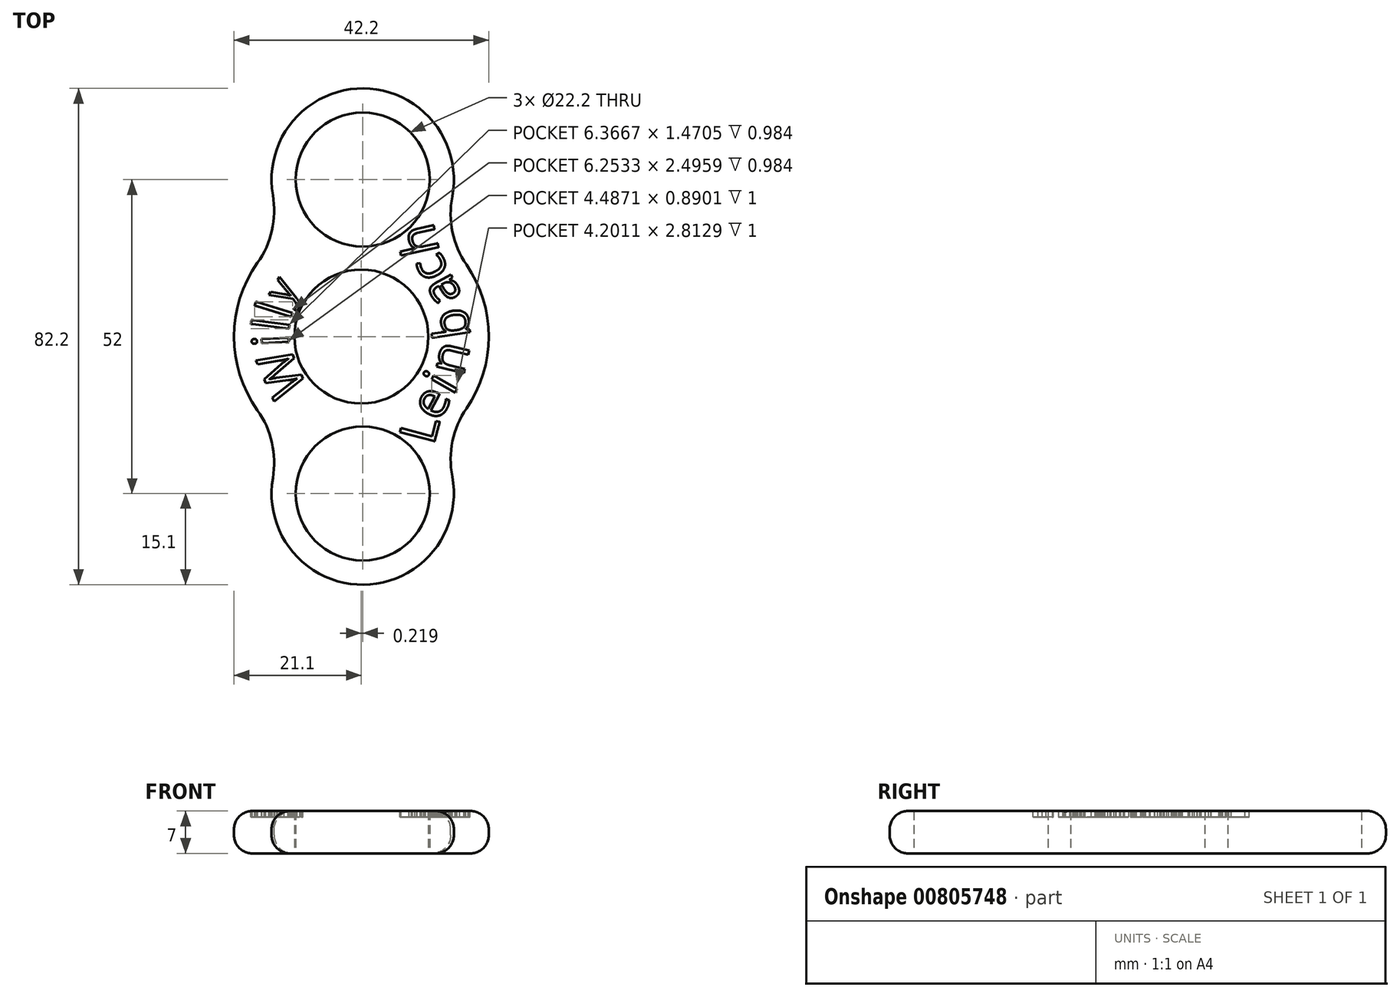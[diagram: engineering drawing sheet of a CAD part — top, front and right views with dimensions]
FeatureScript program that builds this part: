
annotation { "Feature Type Name" : "Feature", "Feature Type Description" : "" }
export const myFeature = defineFeature(function(context is Context, id is Id, definition is map)
    precondition{}
    {
        {
            var Q0;
            Q0=qCreatedBy(makeId("Top.planeOp"),FACE);
            var sketch = newSketch(context, id + "F0", { "sketchPlane" : qUnion([Q0])});
            skCircle(sketch, "E0", {"center": v(0, 0) * mm, "radius": 11.1 * mm});
            skCircle(sketch, "E1", {"center": v(0.22, 26) * mm, "radius": 11.1 * mm});
            skCircle(sketch, "E2", {"center": v(0.22, -26) * mm, "radius": 11.1 * mm});
            skCircle(sketch, "E3.0", {"center": v(0.22, 26) * mm, "radius": 15.1 * mm, "construction": true});
            skCircle(sketch, "E4.0", {"center": v(0.22, -26) * mm, "radius": 15.1 * mm, "construction": true});
            skCircle(sketch, "E5.0", {"center": v(0, 0) * mm, "radius": 21.1 * mm, "construction": true});
            skArc(sketch, "E6", {"start": v(-12.1, 17.28) * mm, "mid": v(0.35, 41.1) * mm, "end": v(12.4, 17.07) * mm});
            skArc(sketch, "E7", {"start": v(12.4, 17.07) * mm, "mid": v(21.1, 0) * mm, "end": v(12.4, -17.07) * mm});
            skArc(sketch, "E8", {"start": v(12.4, -17.07) * mm, "mid": v(0.35, -41.1) * mm, "end": v(-12.1, -17.28) * mm});
            skArc(sketch, "E9", {"start": v(-12.1, -17.28) * mm, "mid": v(-21.1, 0) * mm, "end": v(-12.1, 17.28) * mm});
            skSolve(sketch);
        }
        {
            var Q0;
            Q0=makeQuery(id+"F0.imprint","IMPRINT",FACE,{"disambiguationData":[TD([[makeQuery(id+"F0.imprint","IMPRINT",EDGE,{"derivedFrom":sQuery(id+"F0.wireOp",EDGE,"E0")}),-1.0]])]});
            extrude(context, id + "F1", {"entities" : qUnion([Q0]), "depth" : 7 * mm, "offsetDistance" : 25 * mm});
        }
        {
            var Q0;
            Q0=makeQuery(id+"F1.opExtrude","SWEPT_EDGE",EDGE,{"disambiguationData":[OSD([sQuery(id+"F0.wireOp",EDGE,"E6"),sQuery(id+"F0.wireOp",EDGE,"E9")])]});
            var Q1;
            Q1=makeQuery(id+"F1.opExtrude","SWEPT_EDGE",EDGE,{"disambiguationData":[OSD([sQuery(id+"F0.wireOp",EDGE,"E8"),sQuery(id+"F0.wireOp",EDGE,"E9")])]});
            var Q2;
            Q2=makeQuery(id+"F1.opExtrude","SWEPT_EDGE",EDGE,{"disambiguationData":[OSD([sQuery(id+"F0.wireOp",EDGE,"E7"),sQuery(id+"F0.wireOp",EDGE,"E8")])]});
            var Q3;
            Q3=makeQuery(id+"F1.opExtrude","SWEPT_EDGE",EDGE,{"disambiguationData":[OSD([sQuery(id+"F0.wireOp",EDGE,"E6"),sQuery(id+"F0.wireOp",EDGE,"E7")])]});
            fillet(context, id + "F2", {"entities" : qUnion([Q0, Q1, Q2, Q3]), "radius" : 15 * mm, "tangentPropagation" : true, "allowEdgeOverflow" : false});
        }
        {
            var Q0;
            Q0=makeQuery(id+"F1.opExtrude","CAP_EDGE",EDGE,{"disambiguationData":[OSD([sQuery(id+"F0.wireOp",EDGE,"E9")])],"isStart":false});
            var Q1;
            Q1=makeQuery(id+"F1.opExtrude","CAP_EDGE",EDGE,{"disambiguationData":[OSD([sQuery(id+"F0.wireOp",EDGE,"E7")])],"isStart":true});
            fillet(context, id + "F3", {"entities" : qUnion([Q0, Q1]), "radius" : 3 * mm, "tangentPropagation" : true, "allowEdgeOverflow" : false});
        }
        {
            var Q0;
            Q0=makeQuery(id+"F1.opExtrude","CAP_FACE",FACE,{"disambiguationData":[OSD([sQuery(id+"F0.wireOp",EDGE,"E0"),sQuery(id+"F0.wireOp",EDGE,"E1"),sQuery(id+"F0.wireOp",EDGE,"E2"),sQuery(id+"F0.wireOp",EDGE,"E6"),sQuery(id+"F0.wireOp",EDGE,"E7"),sQuery(id+"F0.wireOp",EDGE,"E8"),sQuery(id+"F0.wireOp",EDGE,"E9")])],"isStart":false});
            var sketch = newSketch(context, id + "F4", { "sketchPlane" : qUnion([Q0])});
            skText(sketch, "E10", { "text": "W", "fontName": "OpenSans-Regular.ttf"});
            skText(sketch, "E11", { "text": "i", "fontName": "OpenSans-Regular.ttf"});
            skText(sketch, "E12", { "text": "l", "fontName": "OpenSans-Regular.ttf"});
            skText(sketch, "E13", { "text": "l", "fontName": "OpenSans-Regular.ttf"});
            skText(sketch, "E14", { "text": "y", "fontName": "OpenSans-Regular.ttf"});
            const initialGuessF4  = {"E10": [-0.00898, -0.00847, -0.40537, 0.91415, 0.006], "E11": [-0.01201, -0.00158, -0.04824, 0.99884, 0.006], "E12": [-0.0121, 0.00057, 0.12637, 0.99198, 0.006], "E13": [-0.01183, 0.0026, 0.2921, 0.9564, 0.006], "E14": [-0.01215, 0.005, 0.50986, 0.86026, 0.005]};
            skSetInitialGuess(sketch, initialGuessF4);
            skSolve(sketch);
        }
        {
            var Q0;
            Q0=makeQuery(id+"F4.imprint","IMPRINT",FACE,{"disambiguationData":[TD([[makeQuery(id+"F4.imprint","IMPRINT",EDGE,{"derivedFrom":sQuery(id+"F4.wireOp",EDGE,"E10.sketch_text.stroke-0")}),-1.0]])]});
            var Q1;
            Q1=makeQuery(id+"F4.imprint","IMPRINT",FACE,{"disambiguationData":[TD([[makeQuery(id+"F4.imprint","IMPRINT",EDGE,{"derivedFrom":sQuery(id+"F4.wireOp",EDGE,"E11.sketch_text.stroke-0")}),-1.0]])]});
            var Q2;
            {var subQ0=sQuery(id+"F4.wireOp",EDGE,"E12.sketch_text.stroke-0");Q2=makeQuery(id+"F4.imprint","IMPRINT",FACE,{"disambiguationData":[TD([[makeQuery(id+"F4.imprint","IMPRINT",EDGE,{"derivedFrom":subQ0}),-1.0]])]});}
            var Q3;
            {var subQ0=sQuery(id+"F4.wireOp",EDGE,"E12.sketch_text.stroke-2");Q3=makeQuery(id+"F4.imprint","IMPRINT",FACE,{"disambiguationData":[TD([[makeQuery(id+"F4.imprint","IMPRINT",EDGE,{"derivedFrom":subQ0}),-1.0]])]});}
            var Q4;
            {var subQ0=sQuery(id+"F4.wireOp",EDGE,"E13.sketch_text.stroke-2");Q4=makeQuery(id+"F4.imprint","IMPRINT",FACE,{"disambiguationData":[TD([[makeQuery(id+"F4.imprint","IMPRINT",EDGE,{"derivedFrom":subQ0}),-1.0]])]});}
            var Q5;
            {var subQ0=sQuery(id+"F4.wireOp",EDGE,"E13.sketch_text.stroke-0");Q5=makeQuery(id+"F4.imprint","IMPRINT",FACE,{"disambiguationData":[TD([[makeQuery(id+"F4.imprint","IMPRINT",EDGE,{"derivedFrom":subQ0}),-1.0]])]});}
            var Q6;
            Q6=makeQuery(id+"F4.imprint","IMPRINT",FACE,{"disambiguationData":[TD([[makeQuery(id+"F4.imprint","IMPRINT",EDGE,{"derivedFrom":sQuery(id+"F4.wireOp",EDGE,"E14.sketch_text.stroke-0")}),-1.0]])]});
            var Q7;
            {var subQ6=sQuery(id+"F4.wireOp",EDGE,"E11.sketch_text.stroke-4");Q7=makeQuery(id+"F4.imprint","IMPRINT",FACE,{"disambiguationData":[TD([[makeQuery(id+"F4.imprint","IMPRINT",EDGE,{"derivedFrom":subQ6}),-1.0]])]});}
            var Q8;
            {var subQ0=sQuery(id+"F4.wireOp",EDGE,"E11.sketch_text.stroke-6");var subQ1=sQuery(id+"F4.wireOp",EDGE,"E11.sketch_text.stroke-5");var subQ2=makeQuery(id+"F4.imprint","INTERSECT",VERTEX,{"derivedFrom":[subQ1,subQ0]});Q8=makeQuery(id+"F4.imprint","IMPRINT",FACE,{"disambiguationData":[TD([[makeQuery(id+"F4.imprint","IMPRINT",EDGE,{"disambiguationData":[TD([[subQ2,1.0]])],"derivedFrom":subQ1}),-1.0]])]});}
            extrude(context, id + "F5", {"entities" : qUnion([Q0, Q1, Q2, Q3, Q4, Q5, Q6, Q7, Q8]), "operationType" : NewBodyOperationType.REMOVE, "oppositeDirection" : true, "depth" : 1 * mm, "offsetDistance" : 25 * mm});
        }
        {
            var Q0;
            Q0=makeQuery(id+"F4.imprint","IMPRINT",FACE,{"disambiguationData":[TD([[makeQuery(id+"F4.imprint","IMPRINT",EDGE,{"derivedFrom":sQuery(id+"F4.wireOp",EDGE,"E10.sketch_text.stroke-0")}),1.0]])]});
            var sketch = newSketch(context, id + "F6", { "sketchPlane" : qUnion([Q0])});
            skText(sketch, "E15", { "text": "L", "fontName": "OpenSans-Regular.ttf"});
            skText(sketch, "E16", { "text": "e", "fontName": "OpenSans-Regular.ttf"});
            skText(sketch, "E17", { "text": "i", "fontName": "OpenSans-Regular.ttf"});
            skText(sketch, "E18", { "text": "n", "fontName": "OpenSans-Regular.ttf"});
            skText(sketch, "E19", { "text": "b", "fontName": "OpenSans-Regular.ttf"});
            skText(sketch, "E20", { "text": "a", "fontName": "OpenSans-Regular.ttf"});
            skText(sketch, "E21", { "text": "c", "fontName": "OpenSans-Regular.ttf"});
            skText(sketch, "E22", { "text": "h", "fontName": "OpenSans-Regular.ttf"});
            const initialGuessF6  = {"E15": [0.01193, -0.01813, 0.25345, 0.96735, 0.006], "E16": [0.01287, -0.01425, 0.46214, 0.8868, 0.006], "E17": [0.01516, -0.0099, 0.49945, 0.86634, 0.006], "E18": [0.01678, -0.00678, 0.23924, 0.97096, 0.00618], "E19": [0.0181, 0, -0.1432, 0.9897, 0.006], "E20": [0.01677, 0.0068, -0.4842, 0.87495, 0.006], "E21": [0.01464, 0.01066, -0.43761, 0.89916, 0.006], "E22": [0.01293, 0.0141, -0.21649, 0.97629, 0.006]};
            skSetInitialGuess(sketch, initialGuessF6);
            skSolve(sketch);
        }
        {
            var Q0;
            Q0 = qSketchRegion(id + "F6", true);
            extrude(context, id + "F7", {"entities" : qUnion([Q0]), "operationType" : NewBodyOperationType.REMOVE, "oppositeDirection" : true, "depth" : 1 * mm, "offsetDistance" : 25 * mm});
        }
    });
